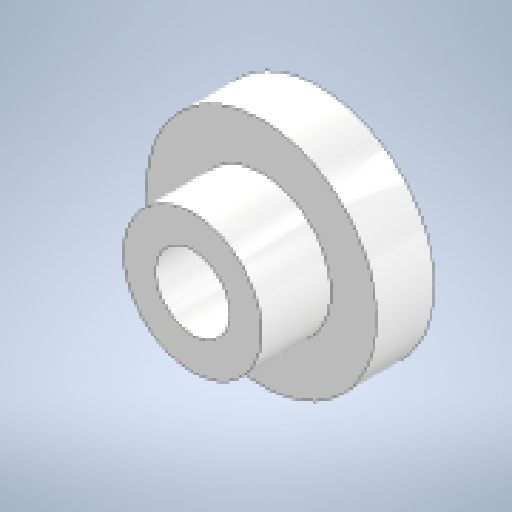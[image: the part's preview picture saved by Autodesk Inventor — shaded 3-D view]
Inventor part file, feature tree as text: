
AUTODESK INVENTOR PART (.ipt)
format: ipt  version: 2025.1 (Build 291241000, 241)  size: 152,064 bytes
history: native  units: mm
features: other x6, sketch x2, extrude x2, reference x1
ambient origin geometry x8: Origin, YZ Plane, XZ Plane, XY Plane, X Axis, Y Axis, Z Axis, Center Point
bodies: Body1 (feature_tree)
feature tree (11):
  other  "ソリッド1"
  sketch  "スケッチ1"
  other  "作業平面1"
  extrude  "押し出し1"  Depth=10.0mm
  sketch  "スケッチ2"
  other  "作業平面2"
  extrude  "押し出し2"  Depth=6.0mm
  reference  "参照1"
  other  "<userpath>\Documents\Inventor\Vixen\doutai.iam"
  other  "doutai.iam"
  other  "namida:1"
